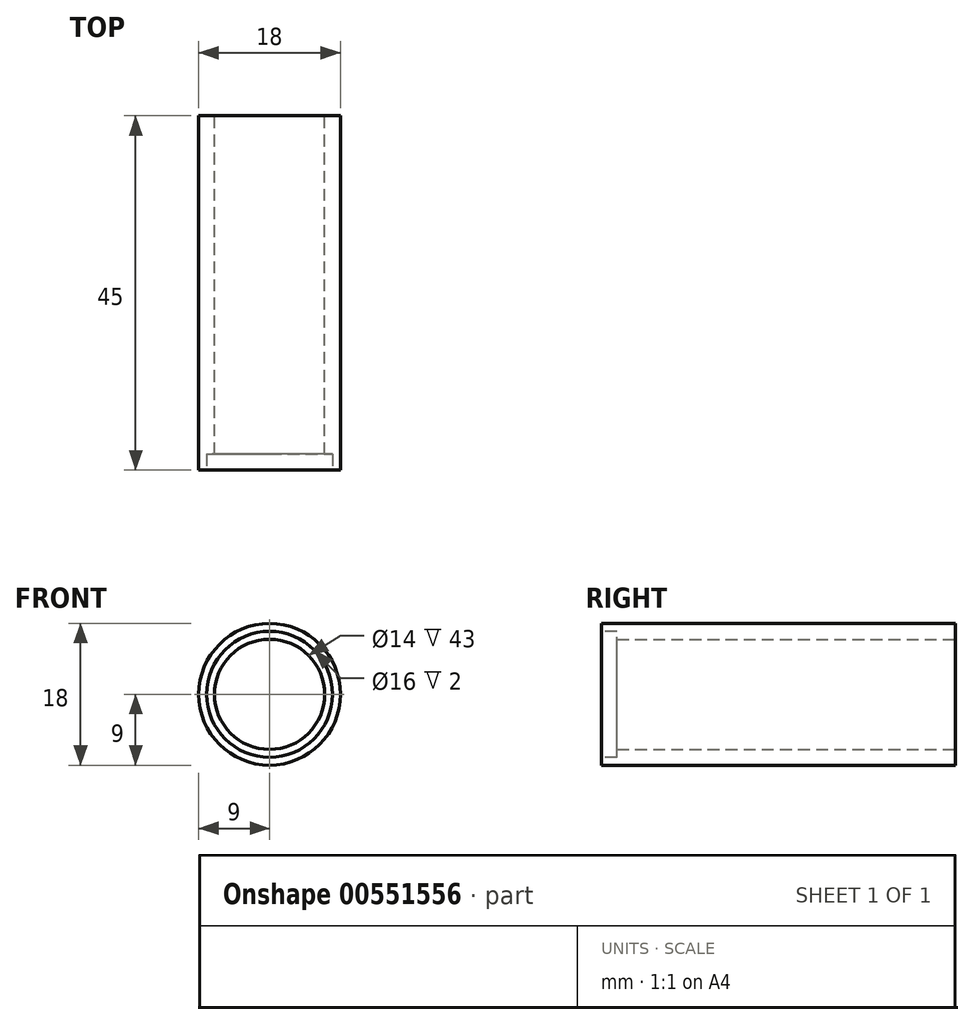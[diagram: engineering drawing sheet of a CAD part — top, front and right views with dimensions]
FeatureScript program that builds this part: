
annotation { "Feature Type Name" : "Feature", "Feature Type Description" : "" }
export const myFeature = defineFeature(function(context is Context, id is Id, definition is map)
    precondition{}
    {
        {
            var Q0;
            Q0=qCreatedBy(makeId("Front.planeOp"),FACE);
            var sketch = newSketch(context, id + "F0", { "sketchPlane" : qUnion([Q0])});
            skCircle(sketch, "E0", {"center": v(0, 0) * mm, "radius": 9 * mm});
            skCircle(sketch, "E1", {"center": v(0, 0) * mm, "radius": 7 * mm});
            skSolve(sketch);
        }
        {
            var Q0;
            Q0 = qSketchRegion(id + "F0", true);
            extrude(context, id + "F1", {"entities" : qUnion([Q0]), "depth" : 45 * mm, "offsetDistance" : 25 * mm});
        }
        {
            var Q0;
            Q0=qCreatedBy(makeId("Front.planeOp"),FACE);
            cPlane(context, id + "F2", {"entities" : qUnion([Q0]), "cplaneType" : CPlaneType.OFFSET, "offset" : 45 * mm, "width" : 150 * mm, "height" : 150 * mm});
        }
        {
            var Q0;
            Q0=qCreatedBy(id+"F2.planeOp",FACE);
            var sketch = newSketch(context, id + "F3", { "sketchPlane" : qUnion([Q0])});
            skCircle(sketch, "E2", {"center": v(0, 0) * mm, "radius": 8 * mm});
            skSolve(sketch);
        }
        {
            var Q0;
            Q0 = qSketchRegion(id + "F3", true);
            extrude(context, id + "F4", {"entities" : qUnion([Q0]), "operationType" : NewBodyOperationType.REMOVE, "oppositeDirection" : true, "depth" : 2 * mm, "offsetDistance" : 25 * mm});
        }
    });
